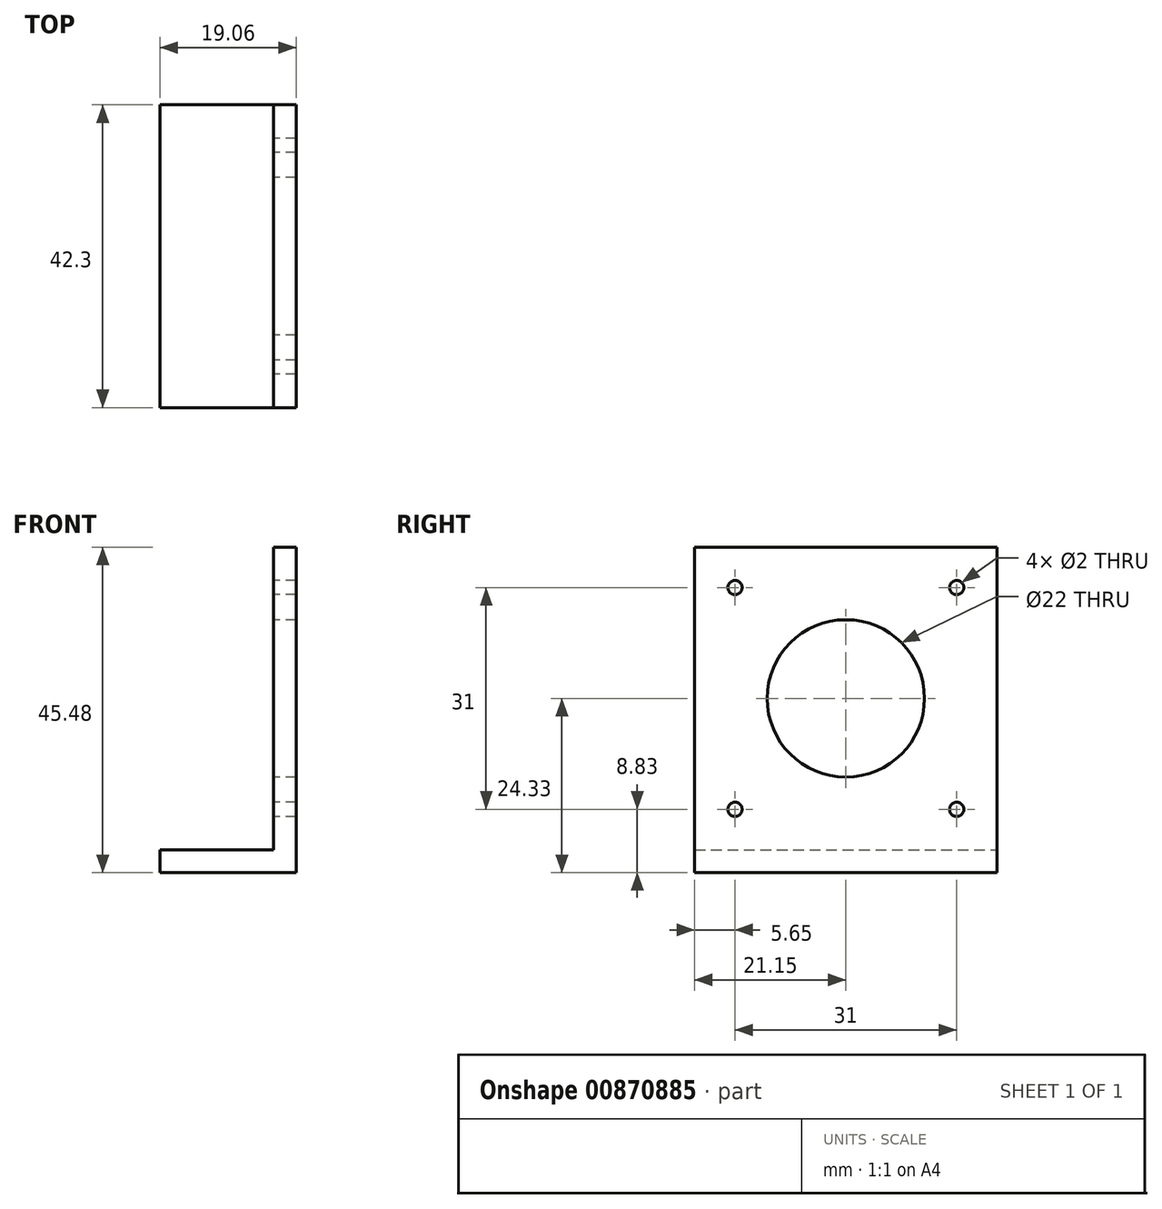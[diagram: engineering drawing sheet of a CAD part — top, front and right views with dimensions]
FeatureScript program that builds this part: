
annotation { "Feature Type Name" : "Feature", "Feature Type Description" : "" }
export const myFeature = defineFeature(function(context is Context, id is Id, definition is map)
    precondition{}
    {
        {
            var Q0;
            Q0=qCreatedBy(makeId("Front.planeOp"),FACE);
            var sketch = newSketch(context, id + "F0", { "sketchPlane" : qUnion([Q0])});
            skLineSegment(sketch, "E0", {"start": v(0, 0) * mm, "end": v(-15.87, 0) * mm});
            skLineSegment(sketch, "E1", {"start": v(-15.87, 0) * mm, "end": v(-15.87, -3.17) * mm});
            skLineSegment(sketch, "E2", {"start": v(-15.87, -3.17) * mm, "end": v(3.18, -3.17) * mm});
            skLineSegment(sketch, "E3", {"start": v(3.18, -3.17) * mm, "end": v(3.18, 42.3) * mm});
            skLineSegment(sketch, "E4", {"start": v(3.18, 42.3) * mm, "end": v(0, 42.3) * mm});
            skLineSegment(sketch, "E5", {"start": v(0, 42.3) * mm, "end": v(0, 0) * mm});
            skSolve(sketch);
        }
        {
            var Q0;
            Q0 = qSketchRegion(id + "F0", true);
            extrude(context, id + "F1", {"entities" : qUnion([Q0]), "depth" : 42.3 * mm, "offsetDistance" : 25 * mm});
        }
        {
            var Q0;
            Q0=qCreatedBy(makeId("Right.planeOp"),FACE);
            var sketch = newSketch(context, id + "F2", { "sketchPlane" : qUnion([Q0])});
            skPoint(sketch, "E6", {"position": v(-21.15, 21.15) * mm});
            skPoint(sketch, "E7", {"position": v(-36.65, 36.65) * mm});
            skPoint(sketch, "E8", {"position": v(-5.65, 36.65) * mm});
            skPoint(sketch, "E9", {"position": v(-5.65, 5.65) * mm});
            skPoint(sketch, "E10", {"position": v(-36.65, 5.65) * mm});
            skCircle(sketch, "E11", {"center": v(-36.65, 36.65) * mm, "radius": 1 * mm});
            skCircle(sketch, "E12", {"center": v(-5.65, 36.65) * mm, "radius": 1 * mm});
            skCircle(sketch, "E13", {"center": v(-5.65, 5.65) * mm, "radius": 1 * mm});
            skCircle(sketch, "E14", {"center": v(-36.65, 5.65) * mm, "radius": 1 * mm});
            skCircle(sketch, "E15", {"center": v(-21.15, 21.15) * mm, "radius": 11 * mm});
            skSolve(sketch);
        }
        {
            var Q0;
            Q0 = qSketchRegion(id + "F2", true);
            extrude(context, id + "F3", {"entities" : qUnion([Q0]), "operationType" : NewBodyOperationType.REMOVE, "endBound" : BoundingType.THROUGH_ALL, "depth" : 25 * mm, "offsetDistance" : 25 * mm});
        }
    });
